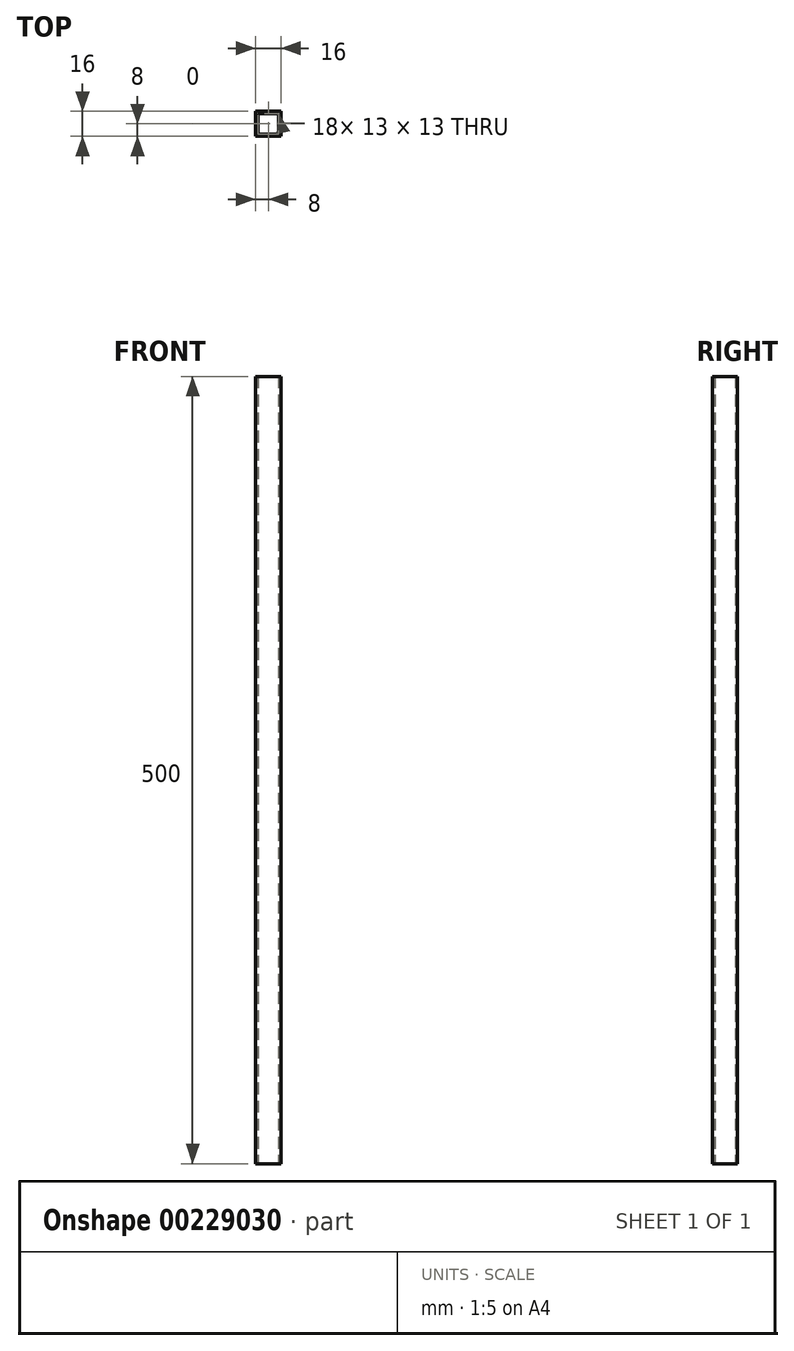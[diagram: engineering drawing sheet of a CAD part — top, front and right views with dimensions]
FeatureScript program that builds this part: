
annotation { "Feature Type Name" : "Feature", "Feature Type Description" : "" }
export const myFeature = defineFeature(function(context is Context, id is Id, definition is map)
    precondition{}
    {
        {
            var Q0;
            Q0=qCreatedBy(makeId("Top.planeOp"),FACE);
            var sketch = newSketch(context, id + "F0", { "sketchPlane" : qUnion([Q0])});
            skLineSegment(sketch, "E0.bottom", {"start": v(0, 0) * mm, "end": v(-13, 0) * mm});
            skLineSegment(sketch, "E0.top", {"start": v(0, 13) * mm, "end": v(-13, 13) * mm});
            skLineSegment(sketch, "E0.left", {"start": v(0, 0) * mm, "end": v(0, 13) * mm});
            skLineSegment(sketch, "E0.right", {"start": v(-13, 0) * mm, "end": v(-13, 13) * mm});
            skLineSegment(sketch, "E1.0", {"start": v(1.5, 14.5) * mm, "end": v(-14.5, 14.5) * mm});
            skLineSegment(sketch, "E1.1", {"start": v(1.5, -1.5) * mm, "end": v(1.5, 14.5) * mm});
            skLineSegment(sketch, "E1.2", {"start": v(1.5, -1.5) * mm, "end": v(-14.5, -1.5) * mm});
            skLineSegment(sketch, "E1.3", {"start": v(-14.5, -1.5) * mm, "end": v(-14.5, 14.5) * mm});
            skSolve(sketch);
        }
        {
            var Q0;
            Q0 = qSketchRegion(id + "F0", true);
            extrude(context, id + "F1", {"entities" : qUnion([Q0]), "depth" : 500 * mm});
        }
    });
